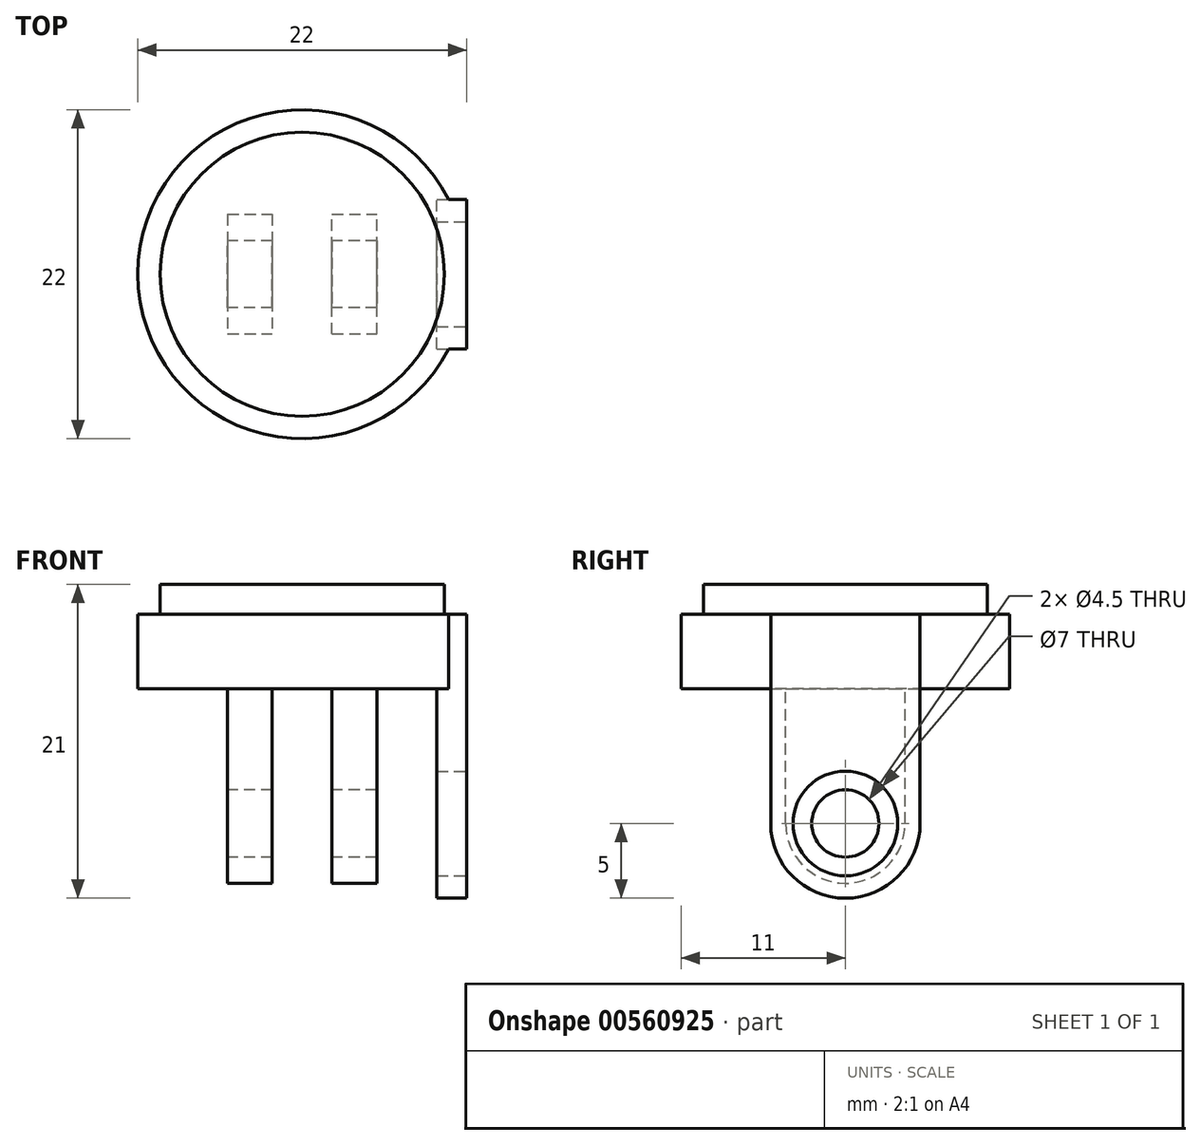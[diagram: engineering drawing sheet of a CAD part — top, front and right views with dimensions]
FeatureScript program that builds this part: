
annotation { "Feature Type Name" : "Feature", "Feature Type Description" : "" }
export const myFeature = defineFeature(function(context is Context, id is Id, definition is map)
    precondition{}
    {
        {
            var Q0;
            Q0=qCreatedBy(makeId("Top.planeOp"),FACE);
            var sketch = newSketch(context, id + "F0", { "sketchPlane" : qUnion([Q0])});
            skCircle(sketch, "E0", {"center": v(0, 0) * mm, "radius": 9.5 * mm});
            skCircle(sketch, "E1", {"center": v(0, 0) * mm, "radius": 11 * mm});
            skLineSegment(sketch, "E2.bottom", {"start": v(-5, 4) * mm, "end": v(-2, 4) * mm});
            skLineSegment(sketch, "E2.top", {"start": v(-5, -4) * mm, "end": v(-2, -4) * mm});
            skLineSegment(sketch, "E2.left", {"start": v(-5, 4) * mm, "end": v(-5, -4) * mm});
            skLineSegment(sketch, "E2.right", {"start": v(-2, 4) * mm, "end": v(-2, -4) * mm});
            skLineSegment(sketch, "E3.bottom", {"start": v(2, -4) * mm, "end": v(5, -4) * mm});
            skLineSegment(sketch, "E3.top", {"start": v(2, 4) * mm, "end": v(5, 4) * mm});
            skLineSegment(sketch, "E3.left", {"start": v(2, -4) * mm, "end": v(2, 4) * mm});
            skLineSegment(sketch, "E3.right", {"start": v(5, -4) * mm, "end": v(5, 4) * mm});
            skLineSegment(sketch, "E4.bottom", {"start": v(9, -5) * mm, "end": v(11, -5) * mm});
            skLineSegment(sketch, "E4.top", {"start": v(9, 5) * mm, "end": v(11, 5) * mm});
            skLineSegment(sketch, "E4.left", {"start": v(9, -5) * mm, "end": v(9, 5) * mm});
            skLineSegment(sketch, "E4.right", {"start": v(11, -5) * mm, "end": v(11, 5) * mm});
            skSolve(sketch);
        }
        {
            var Q0;
            Q0=makeQuery(id+"F0.imprint","IMPRINT",FACE,{"disambiguationData":[TD([[makeQuery(id+"F0.imprint","IMPRINT",EDGE,{"derivedFrom":sQuery(id+"F0.wireOp",EDGE,"E0")}),-1.0]])]});
            var Q1;
            Q1=makeQuery(id+"F0.imprint","IMPRINT",FACE,{"disambiguationData":[TD([[makeQuery(id+"F0.imprint","IMPRINT",EDGE,{"derivedFrom":sQuery(id+"F0.wireOp",EDGE,"E0")}),1.0]])]});
            var Q2;
            Q2=makeQuery(id+"F0.imprint","IMPRINT",FACE,{"disambiguationData":[TD([[makeQuery(id+"F0.imprint","IMPRINT",EDGE,{"derivedFrom":sQuery(id+"F0.wireOp",EDGE,"E2.bottom")}),-1.0]])]});
            var Q3;
            Q3=makeQuery(id+"F0.imprint","IMPRINT",FACE,{"disambiguationData":[TD([[makeQuery(id+"F0.imprint","IMPRINT",EDGE,{"derivedFrom":sQuery(id+"F0.wireOp",EDGE,"E2.bottom")}),1.0]])]});
            var Q4;
            Q4=makeQuery(id+"F0.imprint","IMPRINT",FACE,{"disambiguationData":[TD([[makeQuery(id+"F0.imprint","IMPRINT",EDGE,{"derivedFrom":sQuery(id+"F0.wireOp",EDGE,"E3.bottom")}),1.0]])]});
            var Q5;
            {var subQ0=sQuery(id+"F0.wireOp",EDGE,"E4.left");var subQ9=sQuery(id+"F0.wireOp",EDGE,"E0");var subQ10=makeQuery(id+"F0.imprint","INTERSECT",VERTEX,{"disambiguationData":[OD(0.0)],"derivedFrom":[subQ9,subQ0]});Q5=makeQuery(id+"F0.imprint","IMPRINT",FACE,{"disambiguationData":[TD([[makeQuery(id+"F0.imprint","IMPRINT",EDGE,{"disambiguationData":[TD([[subQ10,-1.0]])],"derivedFrom":subQ9}),-1.0]])]});}
            var Q6;
            {var subQ0=sQuery(id+"F0.wireOp",EDGE,"E4.right");var subQ1=sQuery(id+"F0.wireOp",EDGE,"E1");var subQ2=makeQuery(id+"F0.imprint","INTERSECT",VERTEX,{"derivedFrom":[subQ1,subQ0]});Q6=makeQuery(id+"F0.imprint","IMPRINT",FACE,{"disambiguationData":[TD([[makeQuery(id+"F0.imprint","IMPRINT",EDGE,{"disambiguationData":[TD([[subQ2,1.0]])],"derivedFrom":subQ1}),-1.0]])]});}
            var Q7;
            {var subQ0=sQuery(id+"F0.wireOp",EDGE,"E4.top");var subQ1=sQuery(id+"F0.wireOp",EDGE,"E1");var subQ2=makeQuery(id+"F0.imprint","INTERSECT",VERTEX,{"derivedFrom":[subQ1,subQ0]});Q7=makeQuery(id+"F0.imprint","IMPRINT",FACE,{"disambiguationData":[TD([[makeQuery(id+"F0.imprint","IMPRINT",EDGE,{"disambiguationData":[TD([[subQ2,1.0]])],"derivedFrom":subQ1}),-1.0]])]});}
            extrude(context, id + "F1", {"entities" : qUnion([Q0, Q1, Q2, Q3, Q4, Q5, Q6, Q7]), "oppositeDirection" : true, "depth" : 2 * mm, "offsetDistance" : 25 * mm});
        }
        {
            var Q0;
            Q0=makeQuery(id+"F0.imprint","IMPRINT",FACE,{"disambiguationData":[TD([[makeQuery(id+"F0.imprint","IMPRINT",EDGE,{"derivedFrom":sQuery(id+"F0.wireOp",EDGE,"E0")}),1.0]])]});
            var Q1;
            Q1=makeQuery(id+"F0.imprint","IMPRINT",FACE,{"disambiguationData":[TD([[makeQuery(id+"F0.imprint","IMPRINT",EDGE,{"derivedFrom":sQuery(id+"F0.wireOp",EDGE,"E2.bottom")}),-1.0]])]});
            var Q2;
            Q2=makeQuery(id+"F1.opExtrude","CAP_FACE",FACE,{"disambiguationData":[OSD([sQuery(id+"F0.wireOp",EDGE,"E1"),sQuery(id+"F0.wireOp",EDGE,"E4.bottom"),sQuery(id+"F0.wireOp",EDGE,"E4.top"),sQuery(id+"F0.wireOp",EDGE,"E4.right")])],"isStart":false});
            var Q3;
            Q3=makeQuery(id+"F0.imprint","IMPRINT",FACE,{"disambiguationData":[TD([[makeQuery(id+"F0.imprint","IMPRINT",EDGE,{"derivedFrom":sQuery(id+"F0.wireOp",EDGE,"E3.bottom")}),1.0]])]});
            var Q4;
            Q4=makeQuery(id+"F0.imprint","IMPRINT",FACE,{"disambiguationData":[TD([[makeQuery(id+"F0.imprint","IMPRINT",EDGE,{"derivedFrom":sQuery(id+"F0.wireOp",EDGE,"E2.bottom")}),1.0]])]});
            extrude(context, id + "F2", {"entities" : qUnion([Q0, Q1, Q2, Q3, Q4]), "operationType" : NewBodyOperationType.ADD, "depth" : 5 * mm, "offsetDistance" : 25 * mm});
        }
        {
            var Q0;
            Q0=makeQuery(id+"F0.imprint","IMPRINT",FACE,{"disambiguationData":[TD([[makeQuery(id+"F0.imprint","IMPRINT",EDGE,{"derivedFrom":sQuery(id+"F0.wireOp",EDGE,"E2.bottom")}),-1.0]])]});
            var Q1;
            Q1=makeQuery(id+"F0.imprint","IMPRINT",FACE,{"disambiguationData":[TD([[makeQuery(id+"F0.imprint","IMPRINT",EDGE,{"derivedFrom":sQuery(id+"F0.wireOp",EDGE,"E3.bottom")}),1.0]])]});
            extrude(context, id + "F3", {"entities" : qUnion([Q0, Q1]), "operationType" : NewBodyOperationType.ADD, "oppositeDirection" : true, "depth" : 15 * mm, "offsetDistance" : 25 * mm});
        }
        {
            var Q0;
            Q0=makeQuery(id+"F3.opExtrude","CAP_EDGE",EDGE,{"disambiguationData":[OSD([sQuery(id+"F0.wireOp",EDGE,"E2.bottom")])],"isStart":false});
            var Q1;
            Q1=makeQuery(id+"F3.opExtrude","CAP_EDGE",EDGE,{"disambiguationData":[OSD([sQuery(id+"F0.wireOp",EDGE,"E2.top")])],"isStart":false});
            var Q2;
            Q2=makeQuery(id+"F3.opExtrude","CAP_EDGE",EDGE,{"disambiguationData":[OSD([sQuery(id+"F0.wireOp",EDGE,"E3.bottom")])],"isStart":false});
            var Q3;
            Q3=makeQuery(id+"F3.opExtrude","CAP_EDGE",EDGE,{"disambiguationData":[OSD([sQuery(id+"F0.wireOp",EDGE,"E3.top")])],"isStart":false});
            fillet(context, id + "F4", {"entities" : qUnion([Q0, Q1, Q2, Q3]), "radius" : 4 * mm, "tangentPropagation" : true, "allowEdgeOverflow" : false});
        }
        {
            var Q0;
            Q0=makeQuery(id+"F3.opExtrude","SWEPT_FACE",FACE,{"disambiguationData":[OSD([sQuery(id+"F0.wireOp",EDGE,"E2.right")])]});
            var sketch = newSketch(context, id + "F5", { "sketchPlane" : qUnion([Q0])});
            skCircle(sketch, "E5", {"center": v(0, -11) * mm, "radius": 2.25 * mm});
            skSolve(sketch);
        }
        {
            var Q0;
            Q0=makeQuery(id+"F5.imprint","IMPRINT",FACE,{"disambiguationData":[TD([[makeQuery(id+"F5.imprint","IMPRINT",EDGE,{"derivedFrom":sQuery(id+"F5.wireOp",EDGE,"E5")}),1.0]])]});
            extrude(context, id + "F6", {"entities" : qUnion([Q0]), "operationType" : NewBodyOperationType.REMOVE, "depth" : 50 * mm, "offsetDistance" : 25 * mm, "symmetric" : true});
        }
        {
            var Q0;
            {var subQ0=sQuery(id+"F0.wireOp",EDGE,"E4.right");var subQ1=sQuery(id+"F0.wireOp",EDGE,"E1");var subQ2=makeQuery(id+"F0.imprint","INTERSECT",VERTEX,{"derivedFrom":[subQ1,subQ0]});Q0=makeQuery(id+"F0.imprint","IMPRINT",FACE,{"disambiguationData":[TD([[makeQuery(id+"F0.imprint","IMPRINT",EDGE,{"disambiguationData":[TD([[subQ2,1.0]])],"derivedFrom":subQ1}),-1.0]])]});}
            var Q1;
            {var subQ0=sQuery(id+"F0.wireOp",EDGE,"E4.left");var subQ9=sQuery(id+"F0.wireOp",EDGE,"E0");var subQ10=makeQuery(id+"F0.imprint","INTERSECT",VERTEX,{"disambiguationData":[OD(0.0)],"derivedFrom":[subQ9,subQ0]});Q1=makeQuery(id+"F0.imprint","IMPRINT",FACE,{"disambiguationData":[TD([[makeQuery(id+"F0.imprint","IMPRINT",EDGE,{"disambiguationData":[TD([[subQ10,-1.0]])],"derivedFrom":subQ9}),-1.0]])]});}
            var Q2;
            {var subQ0=sQuery(id+"F0.wireOp",EDGE,"E4.left");var subQ1=sQuery(id+"F0.wireOp",EDGE,"E0");var subQ2=makeQuery(id+"F0.imprint","INTERSECT",VERTEX,{"disambiguationData":[OD(0.0)],"derivedFrom":[subQ1,subQ0]});Q2=makeQuery(id+"F0.imprint","IMPRINT",FACE,{"disambiguationData":[TD([[makeQuery(id+"F0.imprint","IMPRINT",EDGE,{"disambiguationData":[TD([[subQ2,-1.0]])],"derivedFrom":subQ1}),1.0]])]});}
            var Q3;
            {var subQ0=sQuery(id+"F0.wireOp",EDGE,"E4.top");var subQ1=sQuery(id+"F0.wireOp",EDGE,"E1");var subQ2=makeQuery(id+"F0.imprint","INTERSECT",VERTEX,{"derivedFrom":[subQ1,subQ0]});Q3=makeQuery(id+"F0.imprint","IMPRINT",FACE,{"disambiguationData":[TD([[makeQuery(id+"F0.imprint","IMPRINT",EDGE,{"disambiguationData":[TD([[subQ2,1.0]])],"derivedFrom":subQ1}),-1.0]])]});}
            extrude(context, id + "F7", {"entities" : qUnion([Q0, Q1, Q2, Q3]), "operationType" : NewBodyOperationType.ADD, "oppositeDirection" : true, "depth" : 16 * mm, "offsetDistance" : 25 * mm});
        }
        {
            var Q0;
            {var subQ0=sQuery(id+"F0.wireOp",EDGE,"E4.right");Q0=makeQuery(id+"F7.boolean.opBoolean","MERGE",FACE,{"derivedFrom":[makeQuery(id+"F2.boolean.opBoolean","MERGE",FACE,{"derivedFrom":[makeQuery(id+"F1.opExtrude","SWEPT_FACE",FACE,{"disambiguationData":[OSD([subQ0])]}),makeQuery(id+"F2.opExtrude","SWEPT_FACE",FACE,{"disambiguationData":[OSD([subQ0])]})]}),makeQuery(id+"F7.opExtrude","SWEPT_FACE",FACE,{"disambiguationData":[OSD([subQ0])]})]});}
            var sketch = newSketch(context, id + "F8", { "sketchPlane" : qUnion([Q0])});
            skCircle(sketch, "E6", {"center": v(0, -11) * mm, "radius": 3.5 * mm});
            skSolve(sketch);
        }
        {
            var Q0;
            Q0=makeQuery(id+"F8.imprint","IMPRINT",FACE,{"disambiguationData":[TD([[makeQuery(id+"F8.imprint","IMPRINT",EDGE,{"derivedFrom":sQuery(id+"F8.wireOp",EDGE,"E6")}),1.0]])]});
            extrude(context, id + "F9", {"entities" : qUnion([Q0]), "operationType" : NewBodyOperationType.REMOVE, "oppositeDirection" : true, "depth" : 5 * mm, "offsetDistance" : 25 * mm});
        }
        {
            var Q0;
            Q0=makeQuery(id+"F7.opExtrude","CAP_EDGE",EDGE,{"disambiguationData":[OSD([sQuery(id+"F0.wireOp",EDGE,"E4.bottom")])],"isStart":false});
            var Q1;
            Q1=makeQuery(id+"F7.opExtrude","CAP_EDGE",EDGE,{"disambiguationData":[OSD([sQuery(id+"F0.wireOp",EDGE,"E4.top")])],"isStart":false});
            fillet(context, id + "F10", {"entities" : qUnion([Q0, Q1]), "radius" : 5 * mm, "tangentPropagation" : true, "allowEdgeOverflow" : false});
        }
    });
